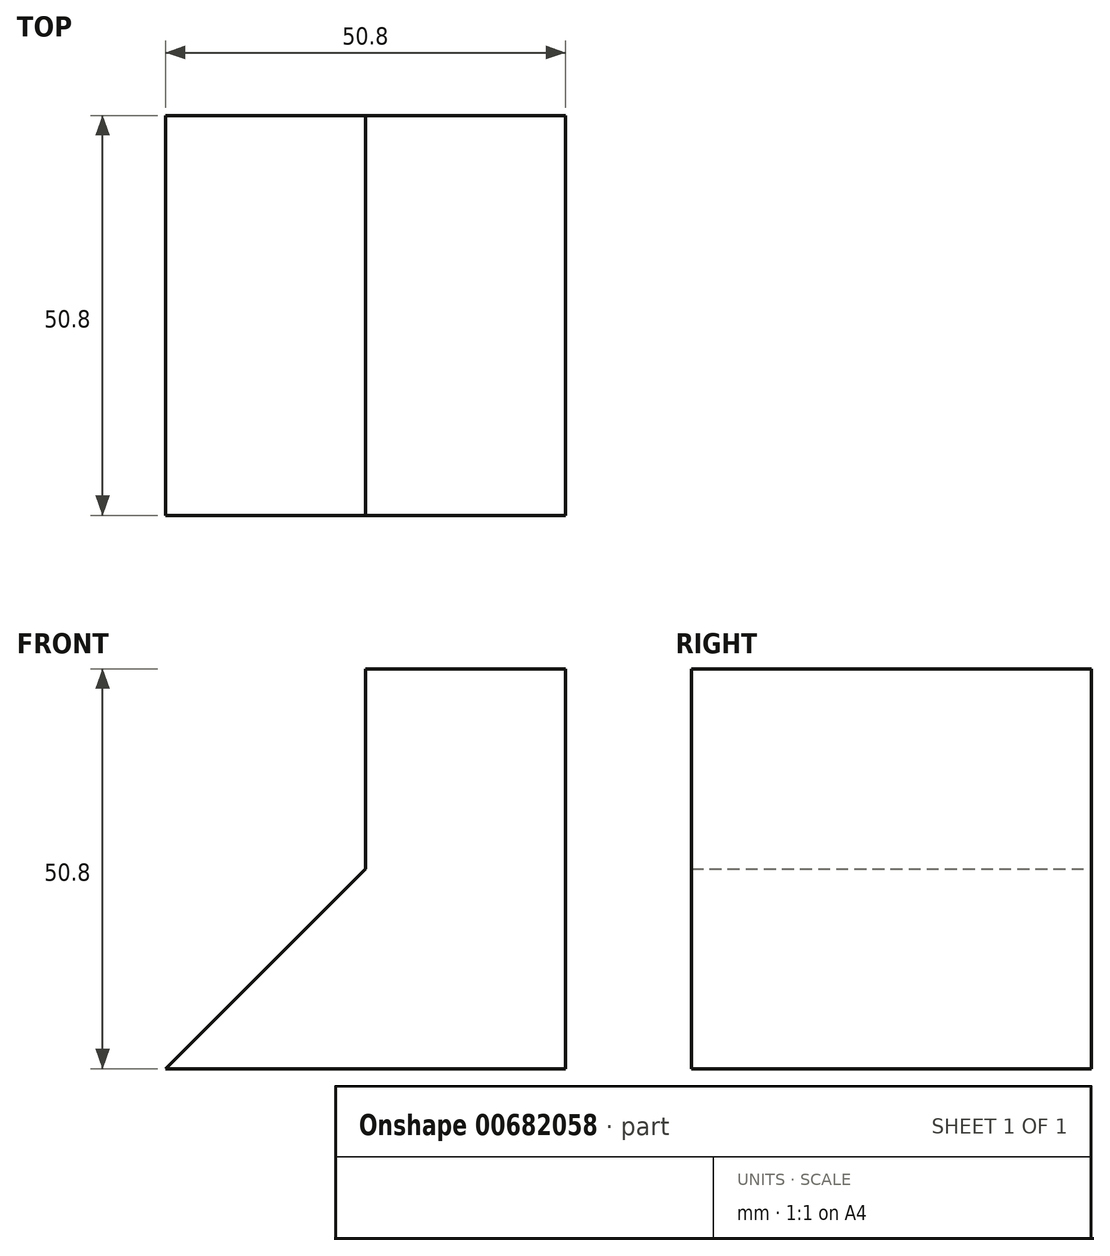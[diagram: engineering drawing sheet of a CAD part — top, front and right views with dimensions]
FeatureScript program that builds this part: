
annotation { "Feature Type Name" : "Feature", "Feature Type Description" : "" }
export const myFeature = defineFeature(function(context is Context, id is Id, definition is map)
    precondition{}
    {
        {
            var Q0;
            Q0=qCreatedBy(makeId("Front.planeOp"),FACE);
            var sketch = newSketch(context, id + "F0", { "sketchPlane" : qUnion([Q0])});
            skLineSegment(sketch, "E0", {"start": v(7.74, 52.61) * mm, "end": v(7.74, 1.81) * mm});
            skLineSegment(sketch, "E1", {"start": v(7.74, 1.81) * mm, "end": v(-43.06, 1.81) * mm});
            skLineSegment(sketch, "E2", {"start": v(7.74, 52.61) * mm, "end": v(-17.66, 52.61) * mm});
            skLineSegment(sketch, "E3", {"start": v(-17.66, 52.61) * mm, "end": v(-17.66, 27.21) * mm});
            skLineSegment(sketch, "E4", {"start": v(-17.66, 27.21) * mm, "end": v(-43.06, 1.81) * mm});
            skSolve(sketch);
        }
        {
            var Q0;
            Q0 = qSketchRegion(id + "F0", true);
            extrude(context, id + "F1", {"entities" : qUnion([Q0]), "depth" : 50.8 * mm, "offsetDistance" : 25.4 * mm});
        }
    });
